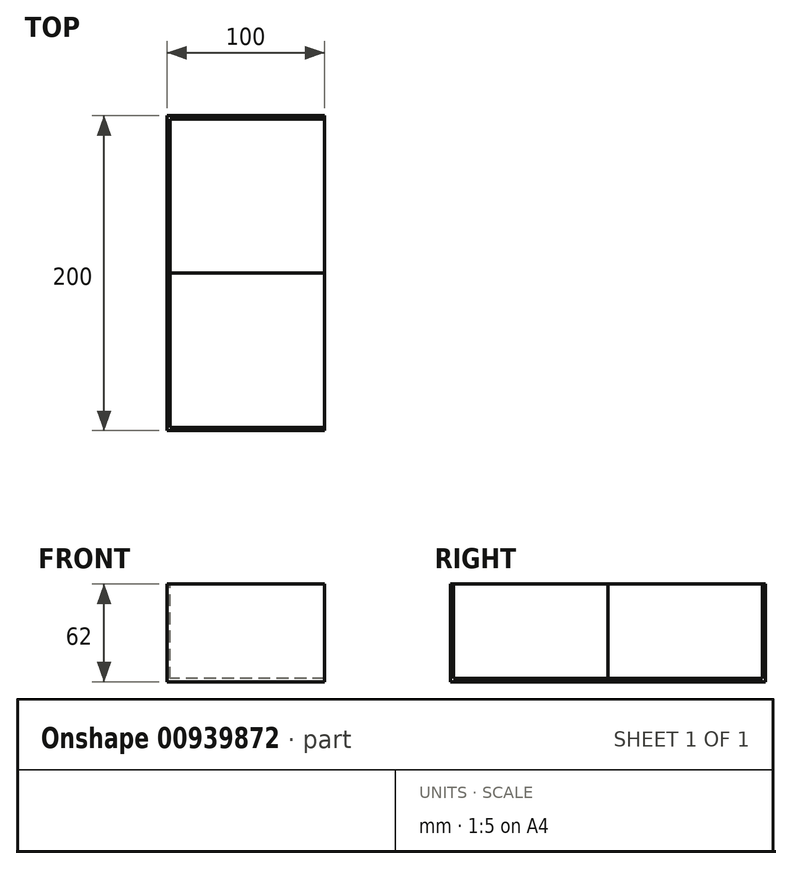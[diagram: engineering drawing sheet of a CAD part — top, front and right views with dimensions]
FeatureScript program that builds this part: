
annotation { "Feature Type Name" : "Feature", "Feature Type Description" : "" }
export const myFeature = defineFeature(function(context is Context, id is Id, definition is map)
    precondition{}
    {
        {
            var Q0;
            Q0=qCreatedBy(makeId("Top.planeOp"),FACE);
            var sketch = newSketch(context, id + "F0", { "sketchPlane" : qUnion([Q0])});
            skLineSegment(sketch, "E0.bottom", {"start": v(-70, 100) * mm, "end": v(-170, 100) * mm});
            skLineSegment(sketch, "E0.top", {"start": v(-70, -100) * mm, "end": v(-170, -100) * mm});
            skLineSegment(sketch, "E0.left", {"start": v(-70, 100) * mm, "end": v(-70, -100) * mm});
            skLineSegment(sketch, "E0.right", {"start": v(-170, 100) * mm, "end": v(-170, -100) * mm});
            skSolve(sketch);
        }
        {
            var Q0;
            Q0=makeQuery(id+"F0.imprint","IMPRINT",FACE,{"disambiguationData":[TD([[makeQuery(id+"F0.imprint","IMPRINT",EDGE,{"derivedFrom":sQuery(id+"F0.wireOp",EDGE,"E0.bottom")}),1.0]])]});
            extrude(context, id + "F1", {"entities" : qUnion([Q0]), "depth" : 62 * mm, "offsetDistance" : 25 * mm});
        }
        {
            var Q0;
            Q0=makeQuery(id+"F1.opExtrude","CAP_FACE",FACE,{"disambiguationData":[OSD([sQuery(id+"F0.wireOp",EDGE,"E0.bottom"),sQuery(id+"F0.wireOp",EDGE,"E0.top"),sQuery(id+"F0.wireOp",EDGE,"E0.left"),sQuery(id+"F0.wireOp",EDGE,"E0.right")])],"isStart":false});
            var sketch = newSketch(context, id + "F2", { "sketchPlane" : qUnion([Q0])});
            skLineSegment(sketch, "E1.bottom", {"start": v(-70, 98) * mm, "end": v(-168, 98) * mm});
            skLineSegment(sketch, "E1.top", {"start": v(-70, -98) * mm, "end": v(-168, -98) * mm});
            skLineSegment(sketch, "E1.left", {"start": v(-70, 98) * mm, "end": v(-70, -98) * mm});
            skLineSegment(sketch, "E1.right", {"start": v(-168, 98) * mm, "end": v(-168, -98) * mm});
            skSolve(sketch);
        }
        {
            var Q0;
            Q0 = qSketchRegion(id + "F2", true);
            extrude(context, id + "F3", {"entities" : qUnion([Q0]), "operationType" : NewBodyOperationType.REMOVE, "oppositeDirection" : true, "depth" : 60 * mm, "offsetDistance" : 25 * mm});
        }
        {
            var Q0;
            Q0=makeQuery(id+"F1.opExtrude","CAP_FACE",FACE,{"disambiguationData":[OSD([sQuery(id+"F0.wireOp",EDGE,"E0.bottom"),sQuery(id+"F0.wireOp",EDGE,"E0.top"),sQuery(id+"F0.wireOp",EDGE,"E0.left"),sQuery(id+"F0.wireOp",EDGE,"E0.right")])],"isStart":true});
            var sketch = newSketch(context, id + "F4", { "sketchPlane" : qUnion([Q0])});
            skLineSegment(sketch, "E2.bottom", {"start": v(-70, 0) * mm, "end": v(-170, 0) * mm});
            skLineSegment(sketch, "E2.top", {"start": v(-70, 0) * mm, "end": v(-170, 0) * mm});
            skLineSegment(sketch, "E2.left", {"start": v(-70, 0) * mm, "end": v(-70, 0) * mm});
            skLineSegment(sketch, "E2.right", {"start": v(-170, 0) * mm, "end": v(-170, 0) * mm});
            skSolve(sketch);
        }
        {
            var Q0;
            Q0 = qSketchRegion(id + "F4", true);
            extrude(context, id + "F5", {"entities" : qUnion([Q0]), "operationType" : NewBodyOperationType.REMOVE, "endBound" : BoundingType.THROUGH_ALL, "oppositeDirection" : true, "depth" : 25 * mm, "offsetDistance" : 25 * mm});
        }
    });
